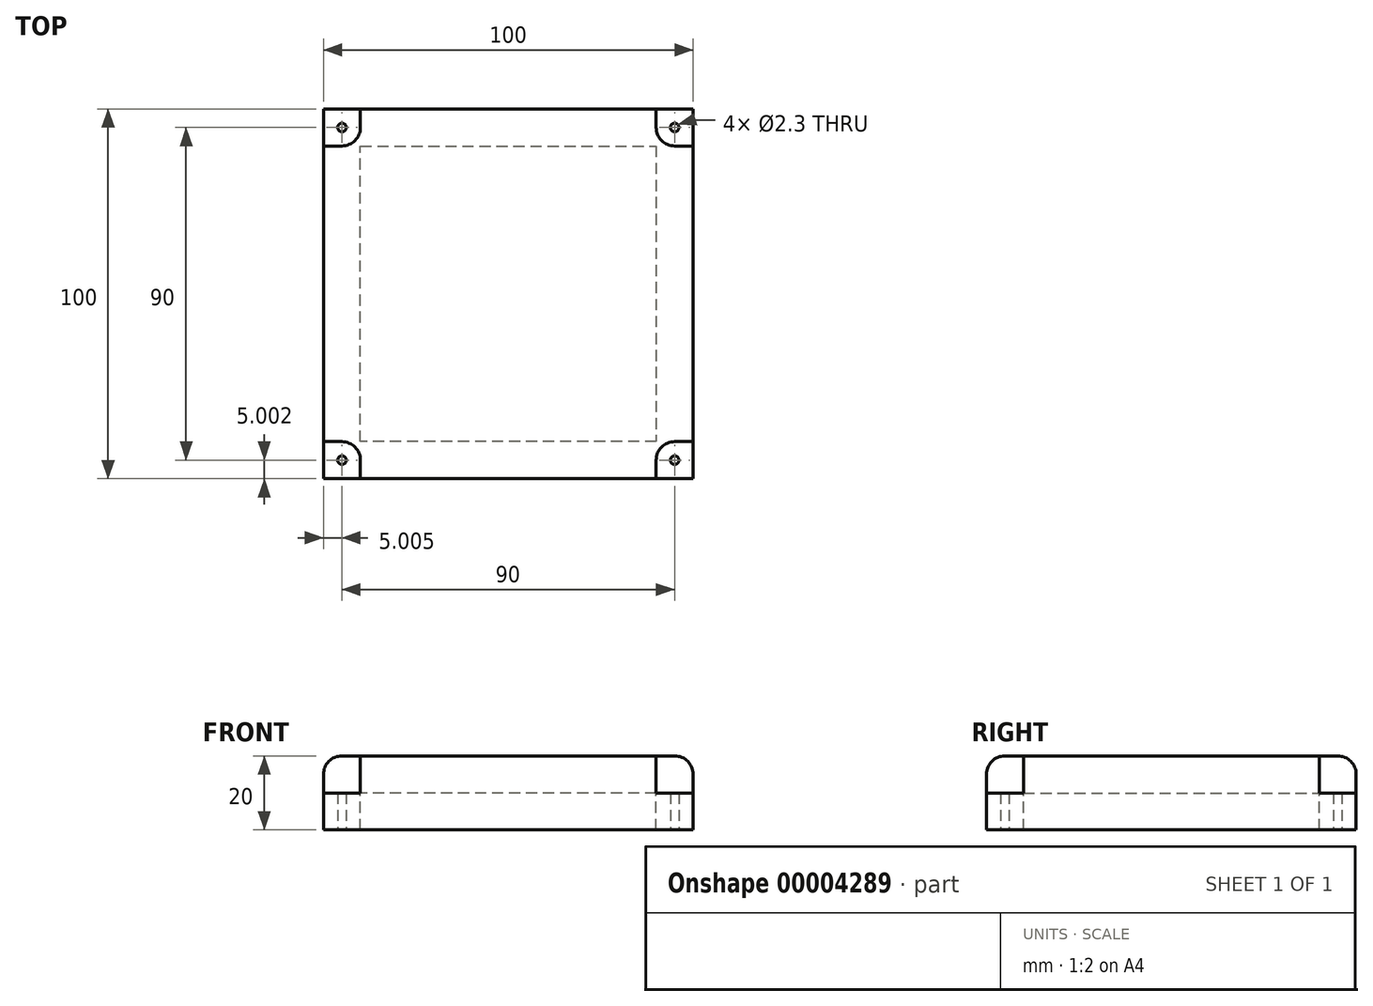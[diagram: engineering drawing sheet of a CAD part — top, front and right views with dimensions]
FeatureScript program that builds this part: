
annotation { "Feature Type Name" : "Feature", "Feature Type Description" : "" }
export const myFeature = defineFeature(function(context is Context, id is Id, definition is map)
    precondition{}
    {
        {
            var Q0;
            Q0=qCreatedBy(makeId("Top.planeOp"),FACE);
            var sketch = newSketch(context, id + "F0", { "sketchPlane" : qUnion([Q0])});
            skLineSegment(sketch, "E0", {"start": v(-95.79, 28.72) * mm, "end": v(4.21, 28.72) * mm});
            skLineSegment(sketch, "E1", {"start": v(4.21, 28.72) * mm, "end": v(4.21, -71.28) * mm});
            skLineSegment(sketch, "E2", {"start": v(4.21, -71.28) * mm, "end": v(-95.79, -71.28) * mm});
            skLineSegment(sketch, "E3", {"start": v(-95.79, -71.28) * mm, "end": v(-95.79, 28.72) * mm});
            skLineSegment(sketch, "E4.0", {"start": v(-85.79, -61.28) * mm, "end": v(-85.79, 18.72) * mm});
            skLineSegment(sketch, "E4.1", {"start": v(-5.79, -61.28) * mm, "end": v(-85.79, -61.28) * mm});
            skLineSegment(sketch, "E4.2", {"start": v(-5.79, 18.72) * mm, "end": v(-5.79, -61.28) * mm});
            skLineSegment(sketch, "E4.3", {"start": v(-85.79, 18.72) * mm, "end": v(-5.79, 18.72) * mm});
            skCircle(sketch, "E5", {"center": v(-0.79, 23.72) * mm, "radius": 1.15 * mm});
            skCircle(sketch, "E6", {"center": v(-0.79, -66.28) * mm, "radius": 1.15 * mm});
            skCircle(sketch, "E7", {"center": v(-90.79, 23.72) * mm, "radius": 1.15 * mm});
            skCircle(sketch, "E8", {"center": v(-90.79, -66.28) * mm, "radius": 1.15 * mm});
            skSolve(sketch);
        }
        {
            var Q0;
            Q0=makeQuery(id+"F0.imprint","IMPRINT",FACE,{"disambiguationData":[TD([[makeQuery(id+"F0.imprint","IMPRINT",EDGE,{"derivedFrom":sQuery(id+"F0.wireOp",EDGE,"E0")}),-1.0]])]});
            var Q1;
            Q1=makeQuery(id+"F0.imprint","IMPRINT",FACE,{"disambiguationData":[TD([[makeQuery(id+"F0.imprint","IMPRINT",EDGE,{"derivedFrom":sQuery(id+"F0.wireOp",EDGE,"E4.0")}),-1.0]])]});
            extrude(context, id + "F1", {"entities" : qUnion([Q0, Q1]), "depth" : 10 * mm});
        }
        {
            var Q0;
            Q0=makeQuery(id+"F0.imprint","IMPRINT",FACE,{"disambiguationData":[TD([[makeQuery(id+"F0.imprint","IMPRINT",EDGE,{"derivedFrom":sQuery(id+"F0.wireOp",EDGE,"E0")}),-1.0]])]});
            extrude(context, id + "F2", {"entities" : qUnion([Q0]), "operationType" : NewBodyOperationType.ADD, "oppositeDirection" : true, "depth" : 10 * mm});
        }
        {
            var Q0;
            Q0=makeQuery(id+"F1.opExtrude","CAP_FACE",FACE,{"disambiguationData":[OSD([sQuery(id+"F0.wireOp",EDGE,"E0"),sQuery(id+"F0.wireOp",EDGE,"E1"),sQuery(id+"F0.wireOp",EDGE,"E2"),sQuery(id+"F0.wireOp",EDGE,"E3"),sQuery(id+"F0.wireOp",EDGE,"E5"),sQuery(id+"F0.wireOp",EDGE,"E6"),sQuery(id+"F0.wireOp",EDGE,"E7"),sQuery(id+"F0.wireOp",EDGE,"E8")])],"isStart":false});
            var sketch = newSketch(context, id + "F3", { "sketchPlane" : qUnion([Q0])});
            skLineSegment(sketch, "E9", {"start": v(-5.79, -66.28) * mm, "end": v(-5.79, -71.28) * mm});
            skLineSegment(sketch, "E10", {"start": v(-0.79, -61.28) * mm, "end": v(4.21, -61.28) * mm});
            skLineSegment(sketch, "E11", {"start": v(-0.79, 18.72) * mm, "end": v(4.21, 18.72) * mm});
            skLineSegment(sketch, "E12", {"start": v(-5.79, 23.72) * mm, "end": v(-5.79, 28.72) * mm});
            skLineSegment(sketch, "E13", {"start": v(-85.79, -66.28) * mm, "end": v(-85.79, -71.28) * mm});
            skLineSegment(sketch, "E14", {"start": v(-90.79, -61.28) * mm, "end": v(-95.79, -61.28) * mm});
            skLineSegment(sketch, "E15", {"start": v(-90.79, 18.72) * mm, "end": v(-95.79, 18.72) * mm});
            skLineSegment(sketch, "E16", {"start": v(-85.79, 23.72) * mm, "end": v(-85.79, 28.72) * mm});
            skPoint(sketch, "E17.visualSharp", {"position": v(-5.79, -61.28) * mm});
            skArc(sketch, "E17.filletArc", {"start": v(-0.79, -61.28) * mm, "mid": v(-4.32, -62.74) * mm, "end": v(-5.79, -66.28) * mm});
            skPoint(sketch, "E18.visualSharp", {"position": v(-85.79, -61.28) * mm});
            skArc(sketch, "E18.filletArc", {"start": v(-85.79, -66.28) * mm, "mid": v(-87.25, -62.74) * mm, "end": v(-90.79, -61.28) * mm});
            skPoint(sketch, "E19.visualSharp", {"position": v(-85.79, 18.72) * mm});
            skArc(sketch, "E19.filletArc", {"start": v(-90.79, 18.72) * mm, "mid": v(-87.25, 20.19) * mm, "end": v(-85.79, 23.72) * mm});
            skPoint(sketch, "E20.visualSharp", {"position": v(-5.79, 18.72) * mm});
            skArc(sketch, "E20.filletArc", {"start": v(-5.79, 23.72) * mm, "mid": v(-4.32, 20.19) * mm, "end": v(-0.79, 18.72) * mm});
            skSolve(sketch);
        }
        {
            var Q0;
            {var subQ1=sQuery(id+"F3.wireOp",EDGE,"E11");Q0=makeQuery(id+"F3.imprint","IMPRINT",FACE,{"disambiguationData":[TD([[makeQuery(id+"F3.imprint","IMPRINT",EDGE,{"derivedFrom":subQ1}),1.0]])]});}
            var Q1;
            {var subQ1=sQuery(id+"F3.wireOp",EDGE,"E15");Q1=makeQuery(id+"F3.imprint","IMPRINT",FACE,{"disambiguationData":[TD([[makeQuery(id+"F3.imprint","IMPRINT",EDGE,{"derivedFrom":subQ1}),-1.0]])]});}
            var Q2;
            {var subQ4=sQuery(id+"F3.wireOp",EDGE,"E13");Q2=makeQuery(id+"F3.imprint","IMPRINT",FACE,{"disambiguationData":[TD([[makeQuery(id+"F3.imprint","IMPRINT",EDGE,{"derivedFrom":subQ4}),-1.0]])]});}
            var Q3;
            {var subQ1=sQuery(id+"F3.wireOp",EDGE,"E9");Q3=makeQuery(id+"F3.imprint","IMPRINT",FACE,{"disambiguationData":[TD([[makeQuery(id+"F3.imprint","IMPRINT",EDGE,{"derivedFrom":subQ1}),1.0]])]});}
            extrude(context, id + "F4", {"entities" : qUnion([Q0, Q1, Q2, Q3]), "operationType" : NewBodyOperationType.REMOVE, "oppositeDirection" : true, "depth" : 10 * mm});
        }
        {
            var Q0;
            Q0=makeQuery(id+"F1.opExtrude","CAP_EDGE",EDGE,{"disambiguationData":[OSD([sQuery(id+"F0.wireOp",EDGE,"E3")])],"isStart":false});
            var Q1;
            Q1=makeQuery(id+"F1.opExtrude","CAP_EDGE",EDGE,{"disambiguationData":[OSD([sQuery(id+"F0.wireOp",EDGE,"E0")])],"isStart":false});
            var Q2;
            Q2=makeQuery(id+"F1.opExtrude","CAP_EDGE",EDGE,{"disambiguationData":[OSD([sQuery(id+"F0.wireOp",EDGE,"E1")])],"isStart":false});
            var Q3;
            Q3=makeQuery(id+"F1.opExtrude","CAP_EDGE",EDGE,{"disambiguationData":[OSD([sQuery(id+"F0.wireOp",EDGE,"E2")])],"isStart":false});
            fillet(context, id + "F5", {"entities" : qUnion([Q0, Q1, Q2, Q3]), "radius" : 5 * mm, "tangentPropagation" : true, "allowEdgeOverflow" : false});
        }
    });
